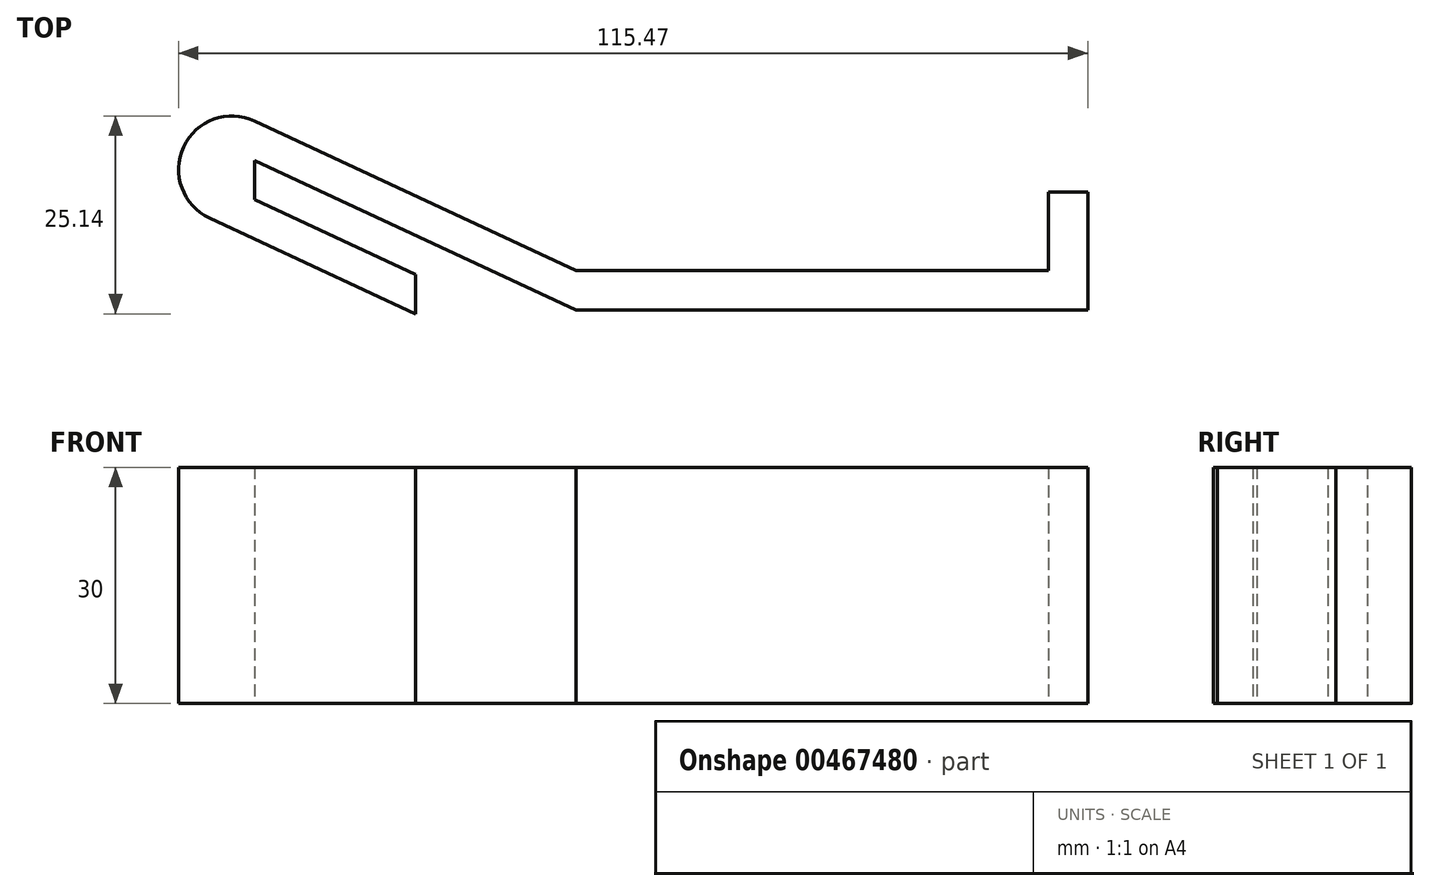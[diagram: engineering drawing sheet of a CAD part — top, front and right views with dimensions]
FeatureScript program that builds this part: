
annotation { "Feature Type Name" : "Feature", "Feature Type Description" : "" }
export const myFeature = defineFeature(function(context is Context, id is Id, definition is map)
    precondition{}
    {
        {
            var Q0;
            Q0=qCreatedBy(makeId("Top.planeOp"),FACE);
            var sketch = newSketch(context, id + "F0", { "sketchPlane" : qUnion([Q0])});
            skLineSegment(sketch, "E0", {"start": v(0, 0) * mm, "end": v(65, 0) * mm});
            skLineSegment(sketch, "E1", {"start": v(65, 0) * mm, "end": v(65, 15) * mm});
            skLineSegment(sketch, "E2", {"start": v(65, 15) * mm, "end": v(60, 15) * mm});
            skLineSegment(sketch, "E3", {"start": v(60, 15) * mm, "end": v(60, 5) * mm});
            skLineSegment(sketch, "E4", {"start": v(60, 5) * mm, "end": v(0, 5) * mm});
            skLineSegment(sketch, "E5", {"start": v(0, 0) * mm, "end": v(-40.8, 19) * mm});
            skLineSegment(sketch, "E6", {"start": v(-40.8, 19) * mm, "end": v(-40.8, 14) * mm});
            skLineSegment(sketch, "E7", {"start": v(-40.8, 14) * mm, "end": v(-20.4, 4.5) * mm});
            skLineSegment(sketch, "E8", {"start": v(0, 5) * mm, "end": v(-40.8, 24) * mm});
            skLineSegment(sketch, "E9", {"start": v(-20.4, 4.5) * mm, "end": v(-20.4, -0.5) * mm});
            skLineSegment(sketch, "E10", {"start": v(-20.4, -0.5) * mm, "end": v(-46.54, 11.67) * mm});
            skArc(sketch, "E11", {"start": v(-40.8, 24) * mm, "mid": v(-49.83, 20.7) * mm, "end": v(-46.54, 11.67) * mm});
            skSolve(sketch);
        }
        {
            var Q0;
            Q0=makeQuery(id+"F0.imprint","IMPRINT",FACE,{"disambiguationData":[TD([[makeQuery(id+"F0.imprint","IMPRINT",EDGE,{"derivedFrom":sQuery(id+"F0.wireOp",EDGE,"E0")}),1.0]])]});
            extrude(context, id + "F1", {"entities" : qUnion([Q0]), "depth" : 30 * mm});
        }
    });
